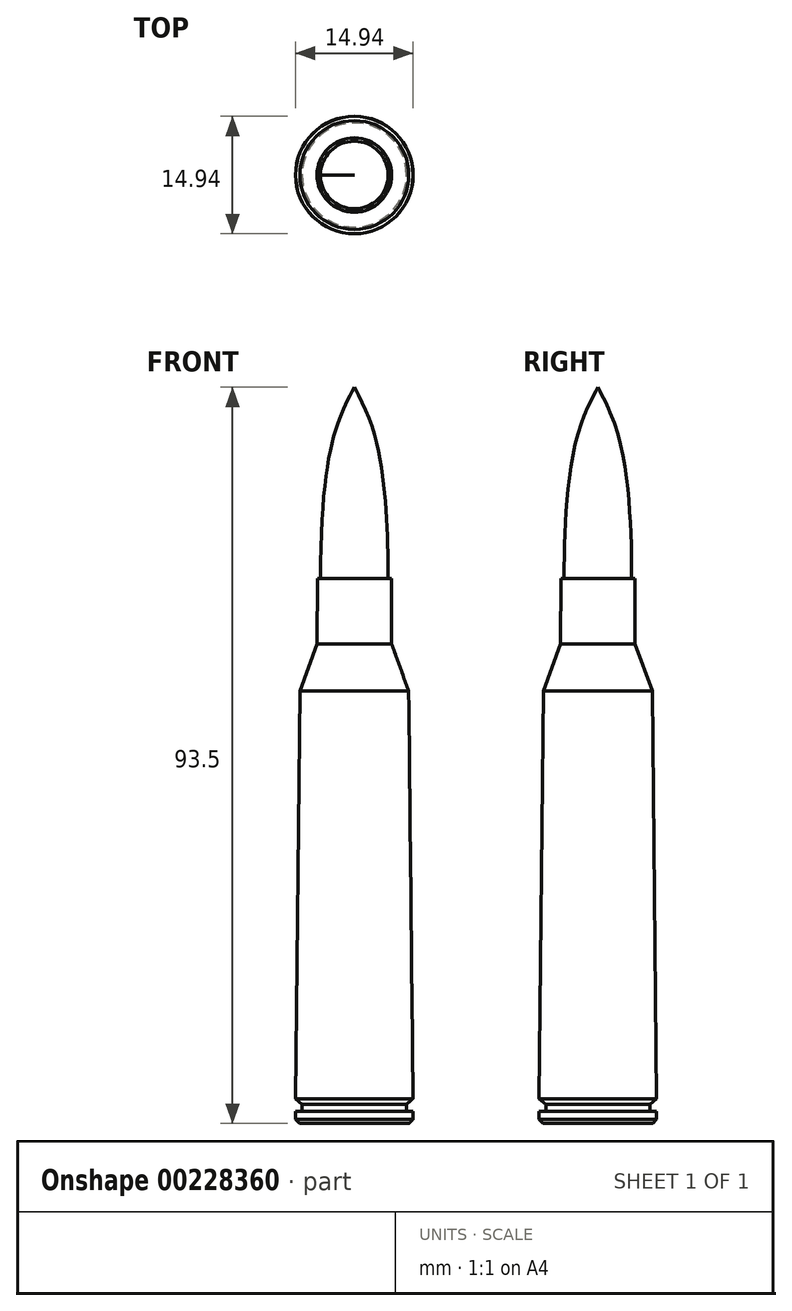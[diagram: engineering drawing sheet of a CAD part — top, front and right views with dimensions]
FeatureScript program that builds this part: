
annotation { "Feature Type Name" : "Feature", "Feature Type Description" : "" }
export const myFeature = defineFeature(function(context is Context, id is Id, definition is map)
    precondition{}
    {
        {
            var Q0;
            Q0=qCreatedBy(makeId("Top.planeOp"),FACE);
            cPlane(context, id + "F0", {"entities" : qUnion([Q0]), "cplaneType" : CPlaneType.OFFSET, "offset" : 60.9 * mm, "oppositeDirection" : true, "width" : 150 * mm, "height" : 150 * mm});
        }
        {
            var Q0;
            Q0=qCreatedBy(makeId("Top.planeOp"),FACE);
            var sketch = newSketch(context, id + "F1", { "sketchPlane" : qUnion([Q0])});
            skCircle(sketch, "E0", {"center": v(0, 0) * mm, "radius": 4.73 * mm});
            skSolve(sketch);
        }
        {
            var Q0;
            Q0=qCreatedBy(id+"F0.planeOp",FACE);
            cPlane(context, id + "F2", {"entities" : qUnion([Q0]), "cplaneType" : CPlaneType.OFFSET, "offset" : 69.2 * mm, "width" : 150 * mm, "height" : 150 * mm});
        }
        {
            var Q0;
            Q0=qCreatedBy(id+"F2.planeOp",FACE);
            var sketch = newSketch(context, id + "F3", { "sketchPlane" : qUnion([Q0])});
            skCircle(sketch, "E1", {"center": v(0, 0) * mm, "radius": 4.7 * mm});
            skCircle(sketch, "E2", {"center": v(0, 0) * mm, "radius": 4.3 * mm});
            skSolve(sketch);
        }
        {
            var Q0;
            Q0=qCreatedBy(id+"F0.planeOp",FACE);
            cPlane(context, id + "F4", {"entities" : qUnion([Q0]), "cplaneType" : CPlaneType.OFFSET, "offset" : 93.5 * mm, "width" : 150 * mm, "height" : 150 * mm});
        }
        {
            var Q0;
            Q0=qCreatedBy(id+"F4.planeOp",FACE);
            var sketch = newSketch(context, id + "F5", { "sketchPlane" : qUnion([Q0])});
            skPoint(sketch, "E3", {"position": v(0, 0) * mm});
            skSolve(sketch);
        }
        {
            var Q0;
            Q0=makeQuery(id+"F3.imprint","IMPRINT",FACE,{"disambiguationData":[TD([[makeQuery(id+"F3.imprint","IMPRINT",EDGE,{"derivedFrom":sQuery(id+"F3.wireOp",EDGE,"E2")}),1.0]])]});
            var Q1;
            Q1=sQuery(id+"F5.wireOp",VERTEX,"E3");
            loft(context, id + "F6", {"startCondition" : LoftEndDerivativeType.NORMAL_TO_PROFILE, "startMagnitude" : 2, "sheetProfilesArray" : [{ "sheetProfileEntities" : qUnion([Q0]) }, { "sheetProfileEntities" : qUnion([Q1]) }]});
        }
        {
            var Q0;
            Q0=qCreatedBy(id+"F2.planeOp",FACE);
            var sketch = newSketch(context, id + "F7", { "sketchPlane" : qUnion([Q0])});
            skCircle(sketch, "E4", {"center": v(0, 0) * mm, "radius": 4.7 * mm});
            skSolve(sketch);
        }
        {
            var Q1;
            Q1=makeQuery(id+"F1.imprint","IMPRINT",FACE,{"disambiguationData":[TD([[makeQuery(id+"F1.imprint","IMPRINT",EDGE,{"derivedFrom":sQuery(id+"F1.wireOp",EDGE,"E0")}),1.0]])]});
            var Q2;
            Q2 = qSketchRegion(id + "F7", true);
            loft(context, id + "F8", {"operationType" : NewBodyOperationType.ADD, "sheetProfilesArray" : [{ "sheetProfileEntities" : qUnion([Q1]) }, { "sheetProfileEntities" : qUnion([Q2]) }]});
        }
        {
            var Q0;
            Q0=qCreatedBy(id+"F0.planeOp",FACE);
            cPlane(context, id + "F9", {"entities" : qUnion([Q0]), "cplaneType" : CPlaneType.OFFSET, "offset" : 54.9 * mm, "width" : 150 * mm, "height" : 150 * mm});
        }
        {
            var Q0;
            Q0=qCreatedBy(id+"F9.planeOp",FACE);
            var sketch = newSketch(context, id + "F10", { "sketchPlane" : qUnion([Q0])});
            skCircle(sketch, "E5", {"center": v(0, 0) * mm, "radius": 6.9 * mm});
            skSolve(sketch);
        }
        {
            var Q1;
            Q1=makeQuery(id+"F1.imprint","IMPRINT",FACE,{"disambiguationData":[TD([[makeQuery(id+"F1.imprint","IMPRINT",EDGE,{"derivedFrom":sQuery(id+"F1.wireOp",EDGE,"E0")}),1.0]])]});
            var Q2;
            Q2=makeQuery(id+"F10.imprint","IMPRINT",FACE,{"disambiguationData":[TD([[makeQuery(id+"F10.imprint","IMPRINT",EDGE,{"derivedFrom":sQuery(id+"F10.wireOp",EDGE,"E5")}),1.0]])]});
            loft(context, id + "F11", {"operationType" : NewBodyOperationType.ADD, "sheetProfilesArray" : [{ "sheetProfileEntities" : qUnion([Q1]) }, { "sheetProfileEntities" : qUnion([Q2]) }]});
        }
        {
            var Q0;
            Q0=qCreatedBy(id+"F0.planeOp",FACE);
            cPlane(context, id + "F12", {"entities" : qUnion([Q0]), "cplaneType" : CPlaneType.OFFSET, "offset" : 3.12 * mm, "width" : 150 * mm, "height" : 150 * mm});
        }
        {
            var Q0;
            Q0=qCreatedBy(id+"F12.planeOp",FACE);
            var sketch = newSketch(context, id + "F13", { "sketchPlane" : qUnion([Q0])});
            skCircle(sketch, "E6", {"center": v(0, 0) * mm, "radius": 7.46 * mm});
            skSolve(sketch);
        }
        {
            var Q1;
            Q1=makeQuery(id+"F13.imprint","IMPRINT",FACE,{"disambiguationData":[TD([[makeQuery(id+"F13.imprint","IMPRINT",EDGE,{"derivedFrom":sQuery(id+"F13.wireOp",EDGE,"E6")}),1.0]])]});
            var Q2;
            Q2=makeQuery(id+"F11.opLoft","CAP_FACE",FACE,{"disambiguationData":[OSD([makeQuery(id+"F10.imprint","IMPRINT",FACE,{"disambiguationData":[TD([[makeQuery(id+"F10.imprint","IMPRINT",EDGE,{"derivedFrom":sQuery(id+"F10.wireOp",EDGE,"E5")}),1.0]])]})])],"isStart":true});
            loft(context, id + "F14", {"operationType" : NewBodyOperationType.ADD, "sheetProfilesArray" : [{ "sheetProfileEntities" : qUnion([Q1]) }, { "sheetProfileEntities" : qUnion([Q2]) }]});
        }
        {
            var Q0;
            Q0=qCreatedBy(id+"F0.planeOp",FACE);
            cPlane(context, id + "F15", {"entities" : qUnion([Q0]), "cplaneType" : CPlaneType.OFFSET, "offset" : 1.52 * mm, "width" : 150 * mm, "height" : 150 * mm});
        }
        {
            var Q0;
            Q0=qCreatedBy(id+"F0.planeOp",FACE);
            cPlane(context, id + "F16", {"entities" : qUnion([Q0]), "cplaneType" : CPlaneType.OFFSET, "offset" : 1.52 * mm, "width" : 150 * mm, "height" : 150 * mm});
        }
        {
            var Q0;
            Q0=qCreatedBy(id+"F15.planeOp",FACE);
            cPlane(context, id + "F17", {"entities" : qUnion([Q0]), "cplaneType" : CPlaneType.OFFSET, "offset" : 0.9 * mm, "width" : 150 * mm, "height" : 150 * mm});
        }
        {
            var Q0;
            Q0=qCreatedBy(id+"F17.planeOp",FACE);
            var sketch = newSketch(context, id + "F18", { "sketchPlane" : qUnion([Q0])});
            skCircle(sketch, "E7", {"center": v(0, 0) * mm, "radius": 6.62 * mm});
            skSolve(sketch);
        }
        {
            var Q1;
            Q1=makeQuery(id+"F14.opLoft","CAP_FACE",FACE,{"disambiguationData":[OSD([makeQuery(id+"F13.imprint","IMPRINT",FACE,{"disambiguationData":[TD([[makeQuery(id+"F13.imprint","IMPRINT",EDGE,{"derivedFrom":sQuery(id+"F13.wireOp",EDGE,"E6")}),1.0]])]})])],"isStart":true});
            var Q2;
            Q2=makeQuery(id+"F18.imprint","IMPRINT",FACE,{"disambiguationData":[TD([[makeQuery(id+"F18.imprint","IMPRINT",EDGE,{"derivedFrom":sQuery(id+"F18.wireOp",EDGE,"E7")}),1.0]])]});
            loft(context, id + "F19", {"operationType" : NewBodyOperationType.ADD, "sheetProfilesArray" : [{ "sheetProfileEntities" : qUnion([Q1]) }, { "sheetProfileEntities" : qUnion([Q2]) }]});
        }
        {
            var Q0;
            Q0=qCreatedBy(id+"F15.planeOp",FACE);
            var sketch = newSketch(context, id + "F20", { "sketchPlane" : qUnion([Q0])});
            skSolve(sketch);
        }
        {
            var Q0;
            Q0 = qSketchRegion(id + "F20", true);
            var Q1;
            Q1=makeQuery(id+"F18.imprint","IMPRINT",FACE,{"disambiguationData":[TD([[makeQuery(id+"F18.imprint","IMPRINT",EDGE,{"derivedFrom":sQuery(id+"F18.wireOp",EDGE,"E7")}),1.0]])]});
            extrude(context, id + "F21", {"entities" : qUnion([Q0, Q1]), "operationType" : NewBodyOperationType.ADD, "oppositeDirection" : true, "depth" : 0.9 * mm});
        }
        {
            var Q0;
            Q0=qCreatedBy(id+"F16.planeOp",FACE);
            var sketch = newSketch(context, id + "F22", { "sketchPlane" : qUnion([Q0])});
            skCircle(sketch, "E8", {"center": v(0, 0) * mm, "radius": 7.47 * mm});
            skSolve(sketch);
        }
        {
            var Q0;
            Q0=makeQuery(id+"F22.imprint","IMPRINT",FACE,{"disambiguationData":[TD([[makeQuery(id+"F22.imprint","IMPRINT",EDGE,{"derivedFrom":sQuery(id+"F22.wireOp",EDGE,"E8")}),1.0]])]});
            extrude(context, id + "F23", {"entities" : qUnion([Q0]), "operationType" : NewBodyOperationType.ADD, "oppositeDirection" : true, "depth" : 1.02 * mm});
        }
        {
            var Q0;
            Q0=qCreatedBy(id+"F0.planeOp",FACE);
            var sketch = newSketch(context, id + "F24", { "sketchPlane" : qUnion([Q0])});
            skCircle(sketch, "E9", {"center": v(0, 0) * mm, "radius": 6.97 * mm});
            skSolve(sketch);
        }
        {
            var Q1;
            Q1=makeQuery(id+"F24.imprint","IMPRINT",FACE,{"disambiguationData":[TD([[makeQuery(id+"F24.imprint","IMPRINT",EDGE,{"derivedFrom":sQuery(id+"F24.wireOp",EDGE,"E9")}),1.0]])]});
            var Q2;
            Q2=makeQuery(id+"F23.opExtrude","CAP_FACE",FACE,{"disambiguationData":[OSD([sQuery(id+"F22.wireOp",EDGE,"E8")])],"isStart":false});
            loft(context, id + "F25", {"operationType" : NewBodyOperationType.ADD, "sheetProfilesArray" : [{ "sheetProfileEntities" : qUnion([Q1]) }, { "sheetProfileEntities" : qUnion([Q2]) }]});
        }
    });
